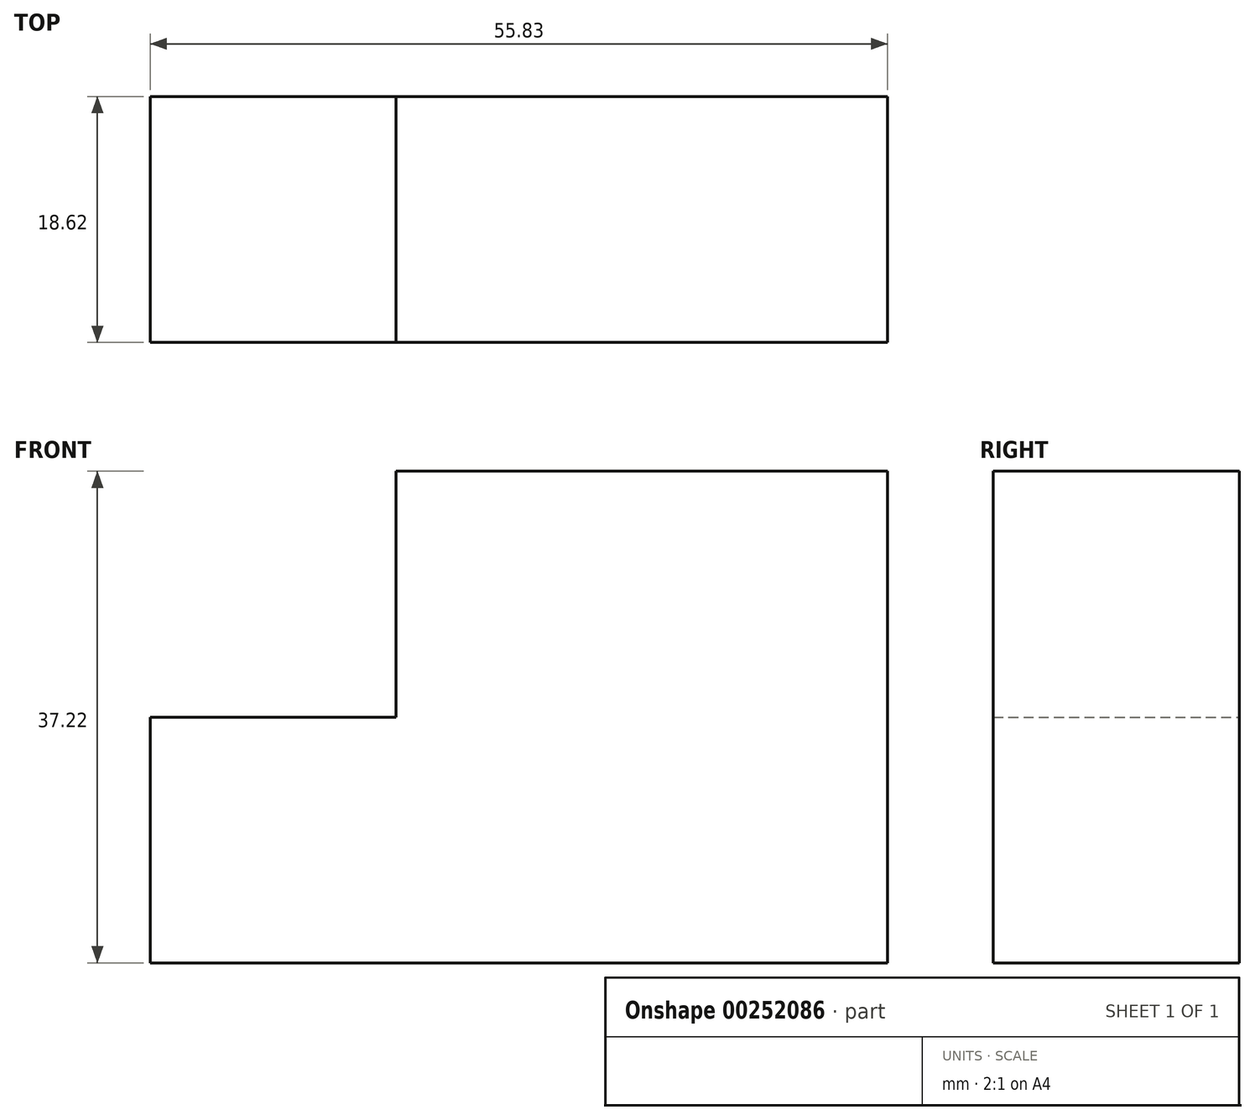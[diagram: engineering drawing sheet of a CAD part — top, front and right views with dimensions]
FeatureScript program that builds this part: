
annotation { "Feature Type Name" : "Feature", "Feature Type Description" : "" }
export const myFeature = defineFeature(function(context is Context, id is Id, definition is map)
    precondition{}
    {
        {
            var Q0;
            Q0=qCreatedBy(makeId("Front.planeOp"),FACE);
            var sketch = newSketch(context, id + "F0", { "sketchPlane" : qUnion([Q0])});
            skLineSegment(sketch, "E0.bottom", {"start": v(-41.02, -14.43) * mm, "end": v(-22.4, -14.43) * mm});
            skLineSegment(sketch, "E0.top", {"start": v(-41.02, 4.18) * mm, "end": v(-22.4, 4.18) * mm});
            skLineSegment(sketch, "E0.left", {"start": v(-41.02, -14.43) * mm, "end": v(-41.02, 4.18) * mm});
            skLineSegment(sketch, "E0.right", {"start": v(-22.4, -14.43) * mm, "end": v(-22.4, 4.18) * mm});
            skLineSegment(sketch, "E1.MirrorCS", {"start": v(-3.8, 4.18) * mm, "end": v(-22.4, 4.18) * mm});
            skLineSegment(sketch, "E2.MirrorCS", {"start": v(-3.8, -14.43) * mm, "end": v(-3.8, 4.18) * mm});
            skLineSegment(sketch, "E3.MirrorCS", {"start": v(-3.8, -14.43) * mm, "end": v(-22.4, -14.43) * mm});
            skLineSegment(sketch, "E4.MirrorCS", {"start": v(-3.8, 4.18) * mm, "end": v(14.81, 4.18) * mm});
            skLineSegment(sketch, "E5.MirrorCS", {"start": v(14.81, -14.43) * mm, "end": v(14.81, 4.18) * mm});
            skLineSegment(sketch, "E6.MirrorCS", {"start": v(-3.8, -14.43) * mm, "end": v(14.81, -14.43) * mm});
            skLineSegment(sketch, "E7.MirrorCS", {"start": v(-41.02, 22.79) * mm, "end": v(-41.02, 4.18) * mm});
            skLineSegment(sketch, "E8.MirrorCS", {"start": v(-41.02, 22.79) * mm, "end": v(-22.4, 22.79) * mm});
            skLineSegment(sketch, "E9.MirrorCS", {"start": v(-22.4, 22.79) * mm, "end": v(-22.4, 4.18) * mm});
            skLineSegment(sketch, "E10.MirrorCS", {"start": v(-3.8, 22.79) * mm, "end": v(-22.4, 22.79) * mm});
            skLineSegment(sketch, "E11.MirrorCS", {"start": v(-3.8, 22.79) * mm, "end": v(-3.8, 4.18) * mm});
            skLineSegment(sketch, "E12.MirrorCS", {"start": v(-3.8, 22.79) * mm, "end": v(14.81, 22.79) * mm});
            skLineSegment(sketch, "E13.MirrorCS", {"start": v(14.81, 22.79) * mm, "end": v(14.81, 4.18) * mm});
            skSolve(sketch);
        }
        {
            var Q0;
            Q0=makeQuery(id+"F0.imprint","IMPRINT",FACE,{"disambiguationData":[TD([[makeQuery(id+"F0.imprint","IMPRINT",EDGE,{"derivedFrom":sQuery(id+"F0.wireOp",EDGE,"E0.bottom")}),1.0]])]});
            var Q1;
            Q1=makeQuery(id+"F0.imprint","IMPRINT",FACE,{"disambiguationData":[TD([[makeQuery(id+"F0.imprint","IMPRINT",EDGE,{"derivedFrom":sQuery(id+"F0.wireOp",EDGE,"E2.MirrorCS")}),-1.0]])]});
            var Q2;
            Q2=makeQuery(id+"F0.imprint","IMPRINT",FACE,{"disambiguationData":[TD([[makeQuery(id+"F0.imprint","IMPRINT",EDGE,{"derivedFrom":sQuery(id+"F0.wireOp",EDGE,"E4.MirrorCS")}),1.0]])]});
            var Q3;
            Q3=makeQuery(id+"F0.imprint","IMPRINT",FACE,{"disambiguationData":[TD([[makeQuery(id+"F0.imprint","IMPRINT",EDGE,{"derivedFrom":sQuery(id+"F0.wireOp",EDGE,"E0.right")}),-1.0]])]});
            var Q4;
            Q4=makeQuery(id+"F0.imprint","IMPRINT",FACE,{"disambiguationData":[TD([[makeQuery(id+"F0.imprint","IMPRINT",EDGE,{"derivedFrom":sQuery(id+"F0.wireOp",EDGE,"E1.MirrorCS")}),-1.0]])]});
            extrude(context, id + "F1", {"entities" : qUnion([Q0, Q1, Q2, Q3, Q4]), "depth" : 18.62 * mm});
        }
    });
